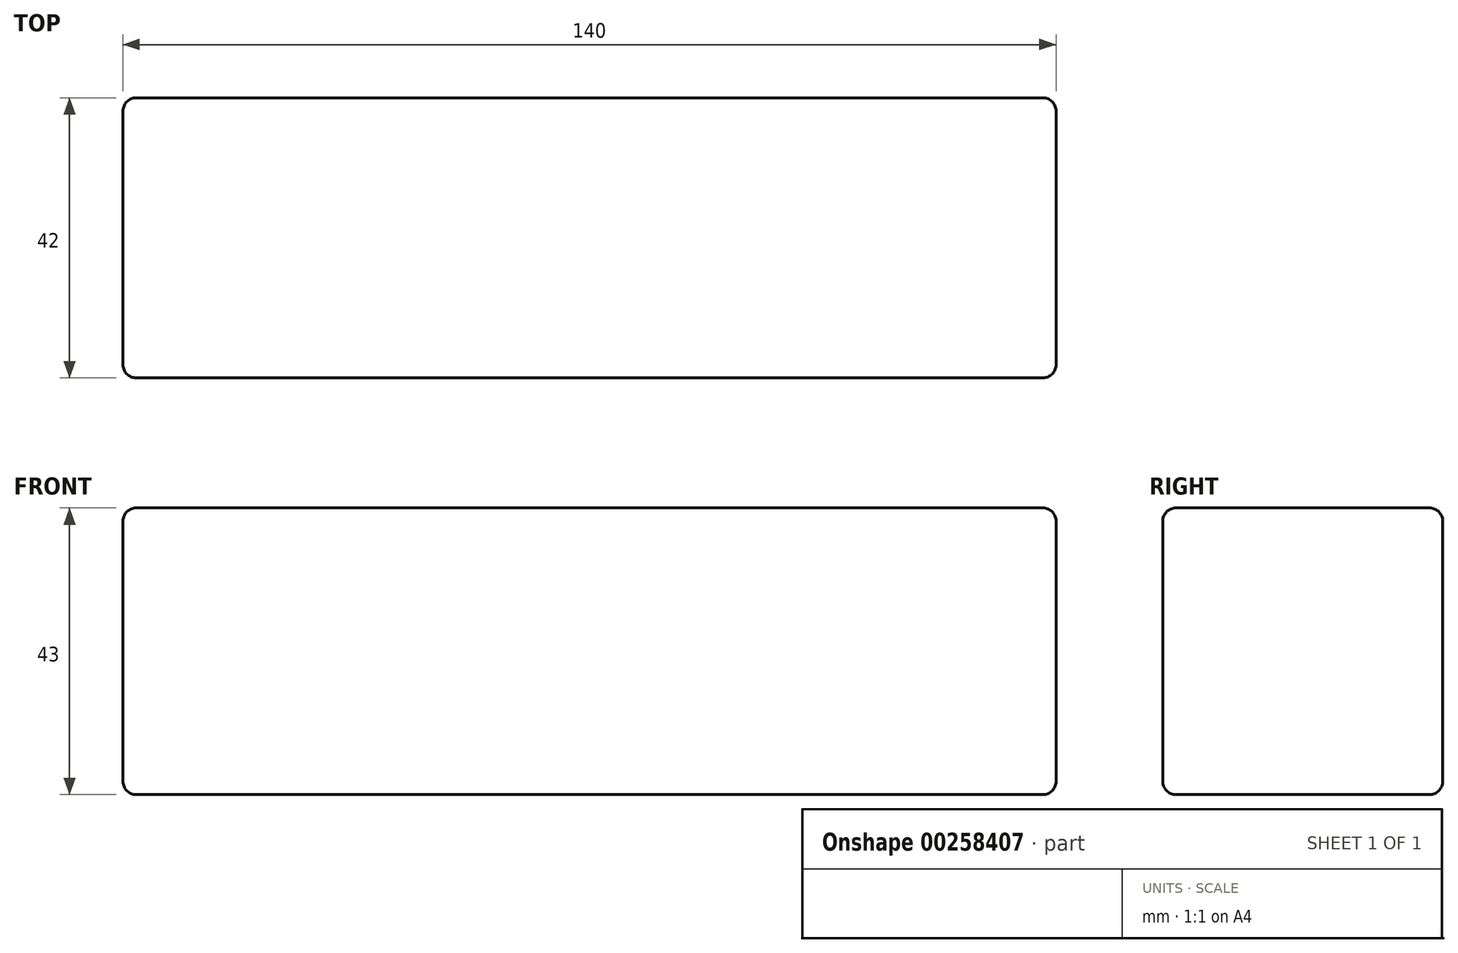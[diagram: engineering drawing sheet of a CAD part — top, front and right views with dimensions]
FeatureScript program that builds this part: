
annotation { "Feature Type Name" : "Feature", "Feature Type Description" : "" }
export const myFeature = defineFeature(function(context is Context, id is Id, definition is map)
    precondition{}
    {
        {
            var Q0;
            Q0=qCreatedBy(makeId("Top.planeOp"),FACE);
            var sketch = newSketch(context, id + "F0", { "sketchPlane" : qUnion([Q0])});
            skLineSegment(sketch, "E0.bottom", {"start": v(70, -21) * mm, "end": v(-70, -21) * mm});
            skLineSegment(sketch, "E0.top", {"start": v(70, 21) * mm, "end": v(-70, 21) * mm});
            skLineSegment(sketch, "E0.left", {"start": v(70, -21) * mm, "end": v(70, 21) * mm});
            skLineSegment(sketch, "E0.right", {"start": v(-70, -21) * mm, "end": v(-70, 21) * mm});
            skPoint(sketch, "E0.middle", {"position": v(0, 0) * mm});
            skSolve(sketch);
        }
        {
            var Q0;
            Q0 = qSketchRegion(id + "F0", true);
            extrude(context, id + "F1", {"entities" : qUnion([Q0]), "depth" : 43 * mm});
        }
        {
            var Q0;
            Q0=makeQuery(id+"F1.opExtrude","SWEPT_FACE",FACE,{"disambiguationData":[OSD([sQuery(id+"F0.wireOp",EDGE,"E0.bottom")])]});
            var Q1;
            Q1=makeQuery(id+"F1.opExtrude","CAP_FACE",FACE,{"disambiguationData":[OSD([sQuery(id+"F0.wireOp",EDGE,"E0.bottom"),sQuery(id+"F0.wireOp",EDGE,"E0.top"),sQuery(id+"F0.wireOp",EDGE,"E0.left"),sQuery(id+"F0.wireOp",EDGE,"E0.right")])],"isStart":false});
            var Q2;
            Q2=makeQuery(id+"F1.opExtrude","SWEPT_FACE",FACE,{"disambiguationData":[OSD([sQuery(id+"F0.wireOp",EDGE,"E0.top")])]});
            var Q3;
            Q3=makeQuery(id+"F1.opExtrude","CAP_FACE",FACE,{"disambiguationData":[OSD([sQuery(id+"F0.wireOp",EDGE,"E0.bottom"),sQuery(id+"F0.wireOp",EDGE,"E0.top"),sQuery(id+"F0.wireOp",EDGE,"E0.left"),sQuery(id+"F0.wireOp",EDGE,"E0.right")])],"isStart":true});
            fillet(context, id + "F2", {"entities" : qUnion([Q0, Q1, Q2, Q3]), "radius" : 2 * mm, "tangentPropagation" : true, "allowEdgeOverflow" : false});
        }
    });
